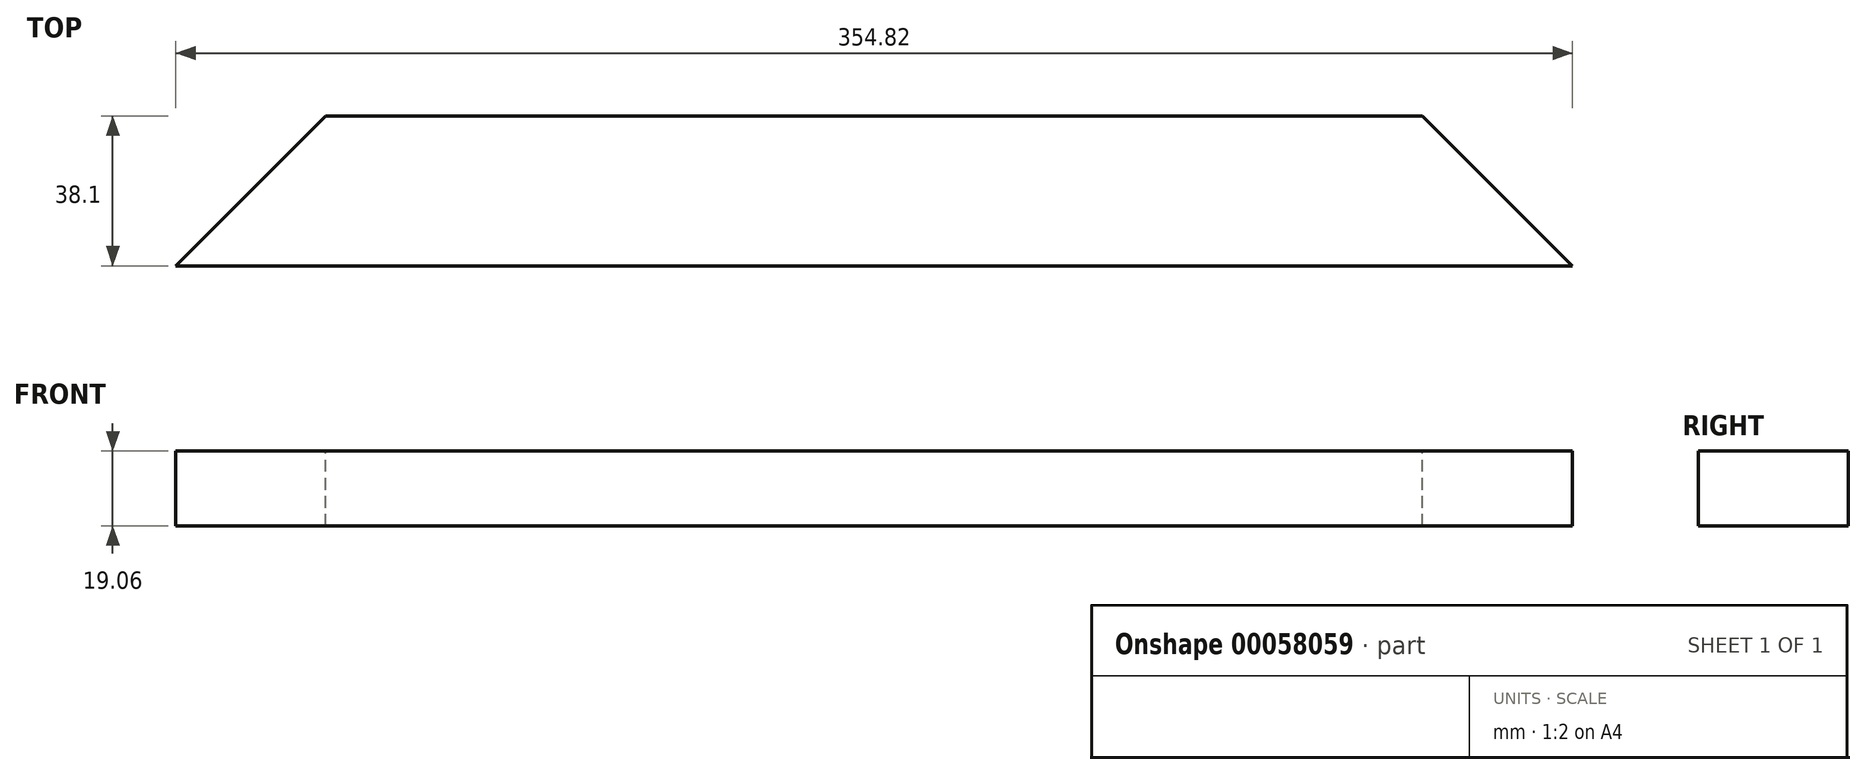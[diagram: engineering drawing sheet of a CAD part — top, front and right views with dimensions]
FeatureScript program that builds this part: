
annotation { "Feature Type Name" : "Feature", "Feature Type Description" : "" }
export const myFeature = defineFeature(function(context is Context, id is Id, definition is map)
    precondition{}
    {
        {
            var Q0;
            Q0=qCreatedBy(makeId("Right.planeOp"),FACE);
            var sketch = newSketch(context, id + "F0", { "sketchPlane" : qUnion([Q0])});
            skLineSegment(sketch, "E0.rect.bottom", {"start": v(19.05, 9.52) * mm, "end": v(-19.05, 9.52) * mm});
            skLineSegment(sketch, "E0.rect.top", {"start": v(19.05, -9.53) * mm, "end": v(-19.05, -9.53) * mm});
            skLineSegment(sketch, "E0.rect.left", {"start": v(19.05, 9.53) * mm, "end": v(19.05, -9.53) * mm});
            skLineSegment(sketch, "E0.rect.right", {"start": v(-19.05, 9.53) * mm, "end": v(-19.05, -9.53) * mm});
            skPoint(sketch, "E0.rect.middle", {"position": v(0, 0) * mm});
            skSolve(sketch);
        }
        {
            var Q0;
            Q0=makeQuery(id+"F0.imprint","IMPRINT",FACE,{"disambiguationData":[TD([[makeQuery(id+"F0.imprint","IMPRINT",EDGE,{"derivedFrom":sQuery(id+"F0.wireOp",EDGE,"E0.rect.bottom")}),1.0]])]});
            extrude(context, id + "F1", {"entities" : qUnion([Q0]), "endBound" : BoundingType.SYMMETRIC, "depth" : 355.6 * mm});
        }
        {
            var Q0;
            Q0=makeQuery(id+"F1.opExtrude","SWEPT_FACE",FACE,{"disambiguationData":[OSD([sQuery(id+"F0.wireOp",EDGE,"E0.rect.bottom")])]});
            var sketch = newSketch(context, id + "F2", { "sketchPlane" : qUnion([Q0])});
            skLineSegment(sketch, "E1", {"start": v(-177.8, -19.05) * mm, "end": v(177.8, -19.05) * mm});
            skSolve(sketch);
        }
        {
            var Q0;
            Q0=makeQuery(id+"F2.imprint","IMPRINT",FACE,{"disambiguationData":[TD([[makeQuery(id+"F2.imprint","IMPRINT",EDGE,{"derivedFrom":sQuery(id+"F2.wireOp",EDGE,"E1")}),-1.0]])]});
            var sketch = newSketch(context, id + "F3", { "sketchPlane" : qUnion([Q0])});
            skLineSegment(sketch, "E2", {"start": v(178.49, -19.29) * mm, "end": v(-178.05, -19.29) * mm});
            skLineSegment(sketch, "E3", {"start": v(-178.05, -19.29) * mm, "end": v(-125.37, 33.4) * mm});
            skLineSegment(sketch, "E4", {"start": v(-125.37, 33.4) * mm, "end": v(125.81, 33.4) * mm});
            skLineSegment(sketch, "E5", {"start": v(125.81, 33.4) * mm, "end": v(178.49, -19.29) * mm});
            skSolve(sketch);
        }
        {
            var Q0;
            {var subQ0=sQuery(id+"F3.wireOp",EDGE,"E3");var subQ1=sQuery(id+"F0.wireOp",EDGE,"E0.rect.bottom");var subQ2=makeQuery(id+"F2.imprint","IMPRINT",EDGE,{"derivedFrom":makeQuery(id+"F1.opExtrude","CAP_EDGE",EDGE,{"disambiguationData":[OSD([subQ1])],"isStart":true})});var subQ3=makeQuery(id+"F3.imprint","INTERSECT",VERTEX,{"derivedFrom":[subQ2,subQ0]});Q0=makeQuery(id+"F3.imprint","IMPRINT",FACE,{"disambiguationData":[TD([[makeQuery(id+"F3.imprint","IMPRINT",EDGE,{"disambiguationData":[TD([[subQ3,-1.0]])],"derivedFrom":subQ0}),1.0]])]});}
            extrude(context, id + "F4", {"entities" : qUnion([Q0]), "operationType" : NewBodyOperationType.REMOVE, "oppositeDirection" : true, "depth" : 50.8 * mm});
        }
        {
            var Q0;
            Q0=makeQuery(id+"F2.imprint","IMPRINT",FACE,{"disambiguationData":[TD([[makeQuery(id+"F2.imprint","IMPRINT",EDGE,{"derivedFrom":sQuery(id+"F2.wireOp",EDGE,"E1")}),-1.0]])]});
            var sketch = newSketch(context, id + "F5", { "sketchPlane" : qUnion([Q0])});
            skLineSegment(sketch, "E6", {"start": v(177.81, -19.84) * mm, "end": v(122.17, 35.8) * mm});
            skLineSegment(sketch, "E7", {"start": v(177.81, -19.84) * mm, "end": v(177.81, 27.68) * mm});
            skLineSegment(sketch, "E8", {"start": v(177.81, 27.68) * mm, "end": v(122.17, 35.8) * mm});
            skSolve(sketch);
        }
        {
            var Q0;
            {var subQ3=sQuery(id+"F0.wireOp",EDGE,"E0.rect.bottom");var subQ6=makeQuery(id+"F2.imprint","IMPRINT",EDGE,{"derivedFrom":makeQuery(id+"F1.opExtrude","CAP_EDGE",EDGE,{"disambiguationData":[OSD([subQ3])],"isStart":false})});Q0=makeQuery(id+"F5.imprint","IMPRINT",FACE,{"disambiguationData":[TD([[makeQuery(id+"F5.imprint","IMPRINT",EDGE,{"derivedFrom":subQ6}),-1.0]])]});}
            extrude(context, id + "F6", {"entities" : qUnion([Q0]), "operationType" : NewBodyOperationType.REMOVE, "oppositeDirection" : true, "depth" : 50.8 * mm});
        }
    });
